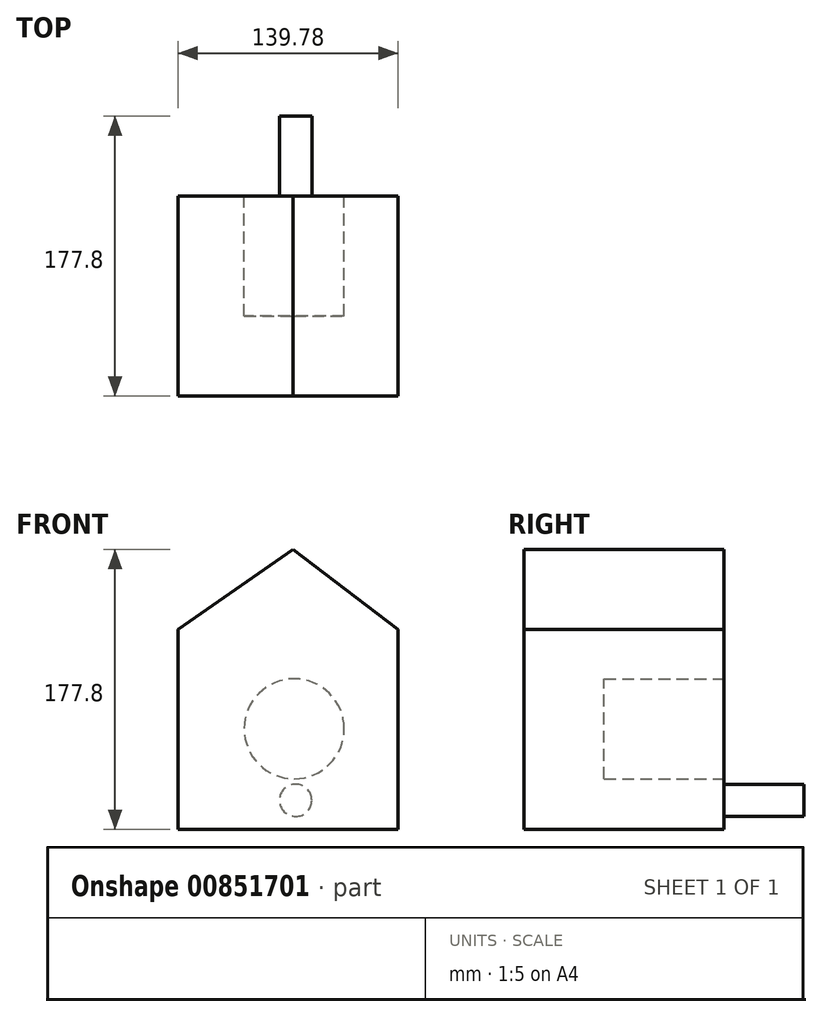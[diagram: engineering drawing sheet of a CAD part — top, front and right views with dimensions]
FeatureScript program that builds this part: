
annotation { "Feature Type Name" : "Feature", "Feature Type Description" : "" }
export const myFeature = defineFeature(function(context is Context, id is Id, definition is map)
    precondition{}
    {
        {
            var Q0;
            Q0=qCreatedBy(makeId("Front.planeOp"),FACE);
            var sketch = newSketch(context, id + "F0", { "sketchPlane" : qUnion([Q0])});
            skLineSegment(sketch, "E0.bottom", {"start": v(0, 0) * mm, "end": v(139.78, 0) * mm});
            skLineSegment(sketch, "E0.top", {"start": v(0, 127) * mm, "end": v(139.78, 127) * mm});
            skLineSegment(sketch, "E0.left", {"start": v(0, 0) * mm, "end": v(0, 127) * mm});
            skLineSegment(sketch, "E0.right", {"start": v(139.78, 0) * mm, "end": v(139.78, 127) * mm});
            skLineSegment(sketch, "E1", {"start": v(139.78, 127) * mm, "end": v(72.96, 177.8) * mm});
            skLineSegment(sketch, "E2", {"start": v(72.96, 177.8) * mm, "end": v(0, 127) * mm});
            skSolve(sketch);
        }
        {
            var Q0;
            Q0=makeQuery(id+"F0.imprint","IMPRINT",FACE,{"disambiguationData":[TD([[makeQuery(id+"F0.imprint","IMPRINT",EDGE,{"derivedFrom":sQuery(id+"F0.wireOp",EDGE,"E0.bottom")}),1.0]])]});
            var Q1;
            Q1=makeQuery(id+"F0.imprint","IMPRINT",FACE,{"disambiguationData":[TD([[makeQuery(id+"F0.imprint","IMPRINT",EDGE,{"derivedFrom":sQuery(id+"F0.wireOp",EDGE,"E0.top")}),1.0]])]});
            extrude(context, id + "F1", {"entities" : qUnion([Q0, Q1]), "depth" : 127 * mm, "offsetDistance" : 25.4 * mm});
        }
        {
            var Q0;
            Q0=qCreatedBy(makeId("Front.planeOp"),FACE);
            var sketch = newSketch(context, id + "F2", { "sketchPlane" : qUnion([Q0])});
            skCircle(sketch, "E3", {"center": v(73.74, 63.92) * mm, "radius": 31.75 * mm});
            skSolve(sketch);
        }
        {
            var Q0;
            Q0=makeQuery(id+"F2.imprint","IMPRINT",FACE,{"disambiguationData":[TD([[makeQuery(id+"F2.imprint","IMPRINT",EDGE,{"derivedFrom":sQuery(id+"F2.wireOp",EDGE,"E3")}),1.0]])]});
            extrude(context, id + "F3", {"entities" : qUnion([Q0]), "depth" : 76.2 * mm, "offsetDistance" : 25.4 * mm});
        }
        {
            var Q0;
            Q0=qCreatedBy(makeId("Front.planeOp"),FACE);
            var sketch = newSketch(context, id + "F4", { "sketchPlane" : qUnion([Q0])});
            skCircle(sketch, "E4", {"center": v(74.66, 18.49) * mm, "radius": 10.26 * mm});
            skSolve(sketch);
        }
        {
            var Q0;
            Q0=makeQuery(id+"F4.imprint","IMPRINT",FACE,{"disambiguationData":[TD([[makeQuery(id+"F4.imprint","IMPRINT",EDGE,{"derivedFrom":sQuery(id+"F4.wireOp",EDGE,"E4")}),1.0]])]});
            extrude(context, id + "F5", {"entities" : qUnion([Q0]), "operationType" : NewBodyOperationType.ADD, "oppositeDirection" : true, "depth" : 50.8 * mm, "offsetDistance" : 25.4 * mm});
        }
    });
